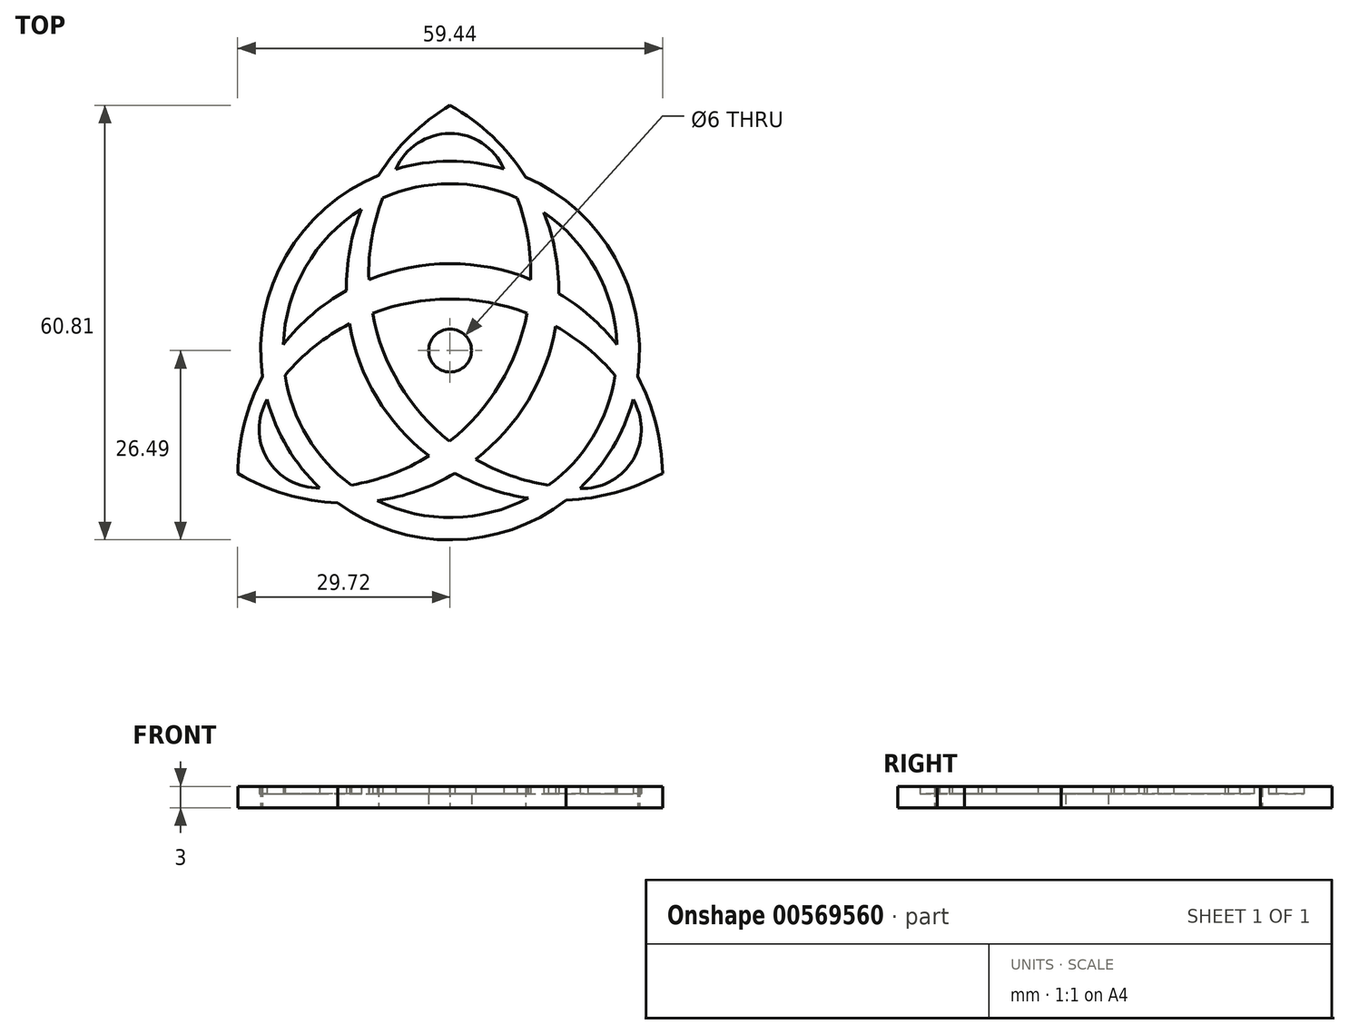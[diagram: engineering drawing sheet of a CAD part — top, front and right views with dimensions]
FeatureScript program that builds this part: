
annotation { "Feature Type Name" : "Feature", "Feature Type Description" : "" }
export const myFeature = defineFeature(function(context is Context, id is Id, definition is map)
    precondition{}
    {
        {
            var Q0;
            Q0=qCreatedBy(makeId("Top.planeOp"),FACE);
            var sketch = newSketch(context, id + "F0", { "sketchPlane" : qUnion([Q0])});
            skCircle(sketch, "E0", {"center": v(37.5, 37.5) * mm, "radius": 3 * mm});
            skArc(sketch, "E1", {"start": v(7.78, 20.34) * mm, "mid": v(14.51, 17.4) * mm, "end": v(21.76, 16.18) * mm});
            skArc(sketch, "E2", {"start": v(37.5, 71.82) * mm, "mid": v(31.92, 67.52) * mm, "end": v(27.5, 62.04) * mm});
            skArc(sketch, "E3", {"start": v(67.22, 20.34) * mm, "mid": v(66.3, 27.32) * mm, "end": v(63.75, 33.9) * mm});
            skArc(sketch, "E4", {"start": v(11.9, 30.65) * mm, "mid": v(14.73, 23.95) * mm, "end": v(19.27, 18.28) * mm});
            skArc(sketch, "E5", {"start": v(14.4, 34.04) * mm, "mid": v(17.5, 25.44) * mm, "end": v(23.68, 18.68) * mm});
            skArc(sketch, "E6.trimOffspring", {"start": v(25.1, 57.28) * mm, "mid": v(17.28, 49.18) * mm, "end": v(14.16, 38.35) * mm});
            skArc(sketch, "E7.trimOffspring", {"start": v(27.5, 62.04) * mm, "mid": v(14.55, 50.75) * mm, "end": v(11.25, 33.9) * mm});
            skArc(sketch, "E8.trimOffspring", {"start": v(46.89, 58.88) * mm, "mid": v(37.46, 60.85) * mm, "end": v(28.05, 58.85) * mm});
            skArc(sketch, "E9.trimOffspring", {"start": v(45.03, 62.9) * mm, "mid": v(37.47, 64) * mm, "end": v(29.91, 62.89) * mm});
            skArc(sketch, "E10.trimOffspring", {"start": v(60.84, 38.35) * mm, "mid": v(57.93, 48.8) * mm, "end": v(50.62, 56.82) * mm});
            skArc(sketch, "E11.trimOffspring", {"start": v(63.75, 33.9) * mm, "mid": v(60.6, 50.47) * mm, "end": v(48.1, 61.79) * mm});
            skArc(sketch, "E12.trimOffspring", {"start": v(51.26, 18.64) * mm, "mid": v(57.47, 25.4) * mm, "end": v(60.6, 34.04) * mm});
            skArc(sketch, "E13.trimOffspring", {"start": v(55.7, 18.24) * mm, "mid": v(60.25, 23.93) * mm, "end": v(63.1, 30.65) * mm});
            skArc(sketch, "E14.trimOffspring", {"start": v(21.76, 16.18) * mm, "mid": v(37.82, 11) * mm, "end": v(53.75, 16.57) * mm});
            skArc(sketch, "E15.trimOffspring", {"start": v(27.33, 16.48) * mm, "mid": v(37.93, 14.15) * mm, "end": v(48.43, 16.86) * mm});
            skArc(sketch, "E16.trimOffspring", {"start": v(11.25, 33.9) * mm, "mid": v(8.7, 27.32) * mm, "end": v(7.78, 20.34) * mm});
            skArc(sketch, "E17.trimOffspring", {"start": v(23.68, 18.68) * mm, "mid": v(29.3, 20.2) * mm, "end": v(34.53, 22.76) * mm});
            skArc(sketch, "E18.trimOffspring", {"start": v(27.33, 16.48) * mm, "mid": v(32.95, 17.88) * mm, "end": v(38.19, 20.34) * mm});
            skArc(sketch, "E19.trimOffspring", {"start": v(53.75, 16.57) * mm, "mid": v(60.7, 17.65) * mm, "end": v(67.22, 20.34) * mm});
            skArc(sketch, "E20.trimOffspring", {"start": v(55.7, 18.24) * mm, "mid": v(56.23, 18.23) * mm, "end": v(56.76, 18.24) * mm});
            skArc(sketch, "E21.trimOffspring", {"start": v(60.6, 34.04) * mm, "mid": v(56.74, 37.83) * mm, "end": v(52.28, 40.87) * mm});
            skArc(sketch, "E22.trimOffspring", {"start": v(60.84, 38.35) * mm, "mid": v(57.1, 42.3) * mm, "end": v(52.7, 45.49) * mm});
            skArc(sketch, "E23.trimOffspring", {"start": v(48.1, 61.79) * mm, "mid": v(43.42, 67.46) * mm, "end": v(37.5, 71.82) * mm});
            skArc(sketch, "E24.trimOffspring", {"start": v(28.05, 58.85) * mm, "mid": v(26.53, 53.22) * mm, "end": v(26.14, 47.4) * mm});
            skArc(sketch, "E25.trimOffspring", {"start": v(25.1, 57.28) * mm, "mid": v(23.48, 51.69) * mm, "end": v(22.98, 45.88) * mm});
            skArc(sketch, "E26.trimOffspring", {"start": v(23.4, 41.25) * mm, "mid": v(27.23, 30.96) * mm, "end": v(34.53, 22.76) * mm});
            skArc(sketch, "E27.trimOffspring", {"start": v(22.98, 45.88) * mm, "mid": v(18.2, 42.55) * mm, "end": v(14.16, 38.35) * mm});
            skArc(sketch, "E28.trimOffspring", {"start": v(26.64, 42.71) * mm, "mid": v(30.43, 32.78) * mm, "end": v(37.43, 24.8) * mm});
            skArc(sketch, "E29.trimOffspring", {"start": v(23.4, 41.25) * mm, "mid": v(18.56, 38.08) * mm, "end": v(14.4, 34.04) * mm});
            skArc(sketch, "E30.trimOffspring", {"start": v(37.43, 24.8) * mm, "mid": v(44.47, 32.8) * mm, "end": v(48.27, 42.74) * mm});
            skArc(sketch, "E31.trimOffspring", {"start": v(41.07, 22.3) * mm, "mid": v(46, 20) * mm, "end": v(51.26, 18.64) * mm});
            skArc(sketch, "E32.trimOffspring", {"start": v(38.19, 20.34) * mm, "mid": v(43.15, 18.13) * mm, "end": v(48.43, 16.86) * mm});
            skArc(sketch, "E33.trimOffspring", {"start": v(41.07, 22.3) * mm, "mid": v(48.43, 30.53) * mm, "end": v(52.28, 40.87) * mm});
            skArc(sketch, "E34.trimOffspring", {"start": v(48.78, 47.44) * mm, "mid": v(37.46, 49.67) * mm, "end": v(26.14, 47.4) * mm});
            skArc(sketch, "E35.trimOffspring", {"start": v(48.27, 42.74) * mm, "mid": v(37.46, 44.72) * mm, "end": v(26.64, 42.71) * mm});
            skArc(sketch, "E36.trimOffspring", {"start": v(48.78, 47.44) * mm, "mid": v(48.4, 53.25) * mm, "end": v(46.89, 58.88) * mm});
            skArc(sketch, "E37.trimOffspring", {"start": v(52.7, 45.49) * mm, "mid": v(52.22, 51.25) * mm, "end": v(50.62, 56.82) * mm});
            skArc(sketch, "E38", {"start": v(56.76, 18.24) * mm, "mid": v(63.36, 22.7) * mm, "end": v(63.1, 30.65) * mm});
            skArc(sketch, "E39", {"start": v(45.03, 62.9) * mm, "mid": v(37.47, 67.88) * mm, "end": v(29.91, 62.89) * mm});
            skArc(sketch, "E40", {"start": v(11.9, 30.65) * mm, "mid": v(11.94, 22.3) * mm, "end": v(19.27, 18.28) * mm});
            skSolve(sketch);
        }
        {
            var Q0;
            Q0=makeQuery(id+"F0.imprint","IMPRINT",FACE,{"disambiguationData":[TD([[makeQuery(id+"F0.imprint","IMPRINT",EDGE,{"derivedFrom":sQuery(id+"F0.wireOp",EDGE,"E1")}),1.0]])]});
            extrude(context, id + "F1", {"entities" : qUnion([Q0]), "depth" : 3 * mm, "offsetDistance" : 25 * mm});
        }
        {
            var Q0;
            Q0=makeQuery(id+"F0.imprint","IMPRINT",FACE,{"disambiguationData":[TD([[makeQuery(id+"F0.imprint","IMPRINT",EDGE,{"derivedFrom":sQuery(id+"F0.wireOp",EDGE,"E5")}),1.0]])]});
            var Q1;
            Q1=makeQuery(id+"F0.imprint","IMPRINT",FACE,{"disambiguationData":[TD([[makeQuery(id+"F0.imprint","IMPRINT",EDGE,{"derivedFrom":sQuery(id+"F0.wireOp",EDGE,"E4")}),-1.0]])]});
            var Q2;
            Q2=makeQuery(id+"F0.imprint","IMPRINT",FACE,{"disambiguationData":[TD([[makeQuery(id+"F0.imprint","IMPRINT",EDGE,{"derivedFrom":sQuery(id+"F0.wireOp",EDGE,"E6.trimOffspring")}),1.0]])]});
            var Q3;
            Q3=makeQuery(id+"F0.imprint","IMPRINT",FACE,{"disambiguationData":[TD([[makeQuery(id+"F0.imprint","IMPRINT",EDGE,{"derivedFrom":sQuery(id+"F0.wireOp",EDGE,"E8.trimOffspring")}),1.0]])]});
            var Q4;
            Q4=makeQuery(id+"F0.imprint","IMPRINT",FACE,{"disambiguationData":[TD([[makeQuery(id+"F0.imprint","IMPRINT",EDGE,{"derivedFrom":sQuery(id+"F0.wireOp",EDGE,"E9.trimOffspring")}),-1.0]])]});
            var Q5;
            Q5=makeQuery(id+"F0.imprint","IMPRINT",FACE,{"disambiguationData":[TD([[makeQuery(id+"F0.imprint","IMPRINT",EDGE,{"derivedFrom":sQuery(id+"F0.wireOp",EDGE,"E10.trimOffspring")}),1.0]])]});
            var Q6;
            Q6=makeQuery(id+"F0.imprint","IMPRINT",FACE,{"disambiguationData":[TD([[makeQuery(id+"F0.imprint","IMPRINT",EDGE,{"derivedFrom":sQuery(id+"F0.wireOp",EDGE,"E12.trimOffspring")}),1.0]])]});
            var Q7;
            Q7=makeQuery(id+"F0.imprint","IMPRINT",FACE,{"disambiguationData":[TD([[makeQuery(id+"F0.imprint","IMPRINT",EDGE,{"derivedFrom":sQuery(id+"F0.wireOp",EDGE,"E15.trimOffspring")}),1.0]])]});
            var Q8;
            Q8=makeQuery(id+"F0.imprint","IMPRINT",FACE,{"disambiguationData":[TD([[makeQuery(id+"F0.imprint","IMPRINT",EDGE,{"derivedFrom":sQuery(id+"F0.wireOp",EDGE,"E13.trimOffspring")}),-1.0]])]});
            var Q9;
            Q9=makeQuery(id+"F0.imprint","IMPRINT",FACE,{"disambiguationData":[TD([[makeQuery(id+"F0.imprint","IMPRINT",EDGE,{"derivedFrom":sQuery(id+"F0.wireOp",EDGE,"E0")}),-1.0]])]});
            extrude(context, id + "F2", {"entities" : qUnion([Q0, Q1, Q2, Q3, Q4, Q5, Q6, Q7, Q8, Q9]), "operationType" : NewBodyOperationType.ADD, "depth" : 2 * mm, "offsetDistance" : 25 * mm});
        }
    });
